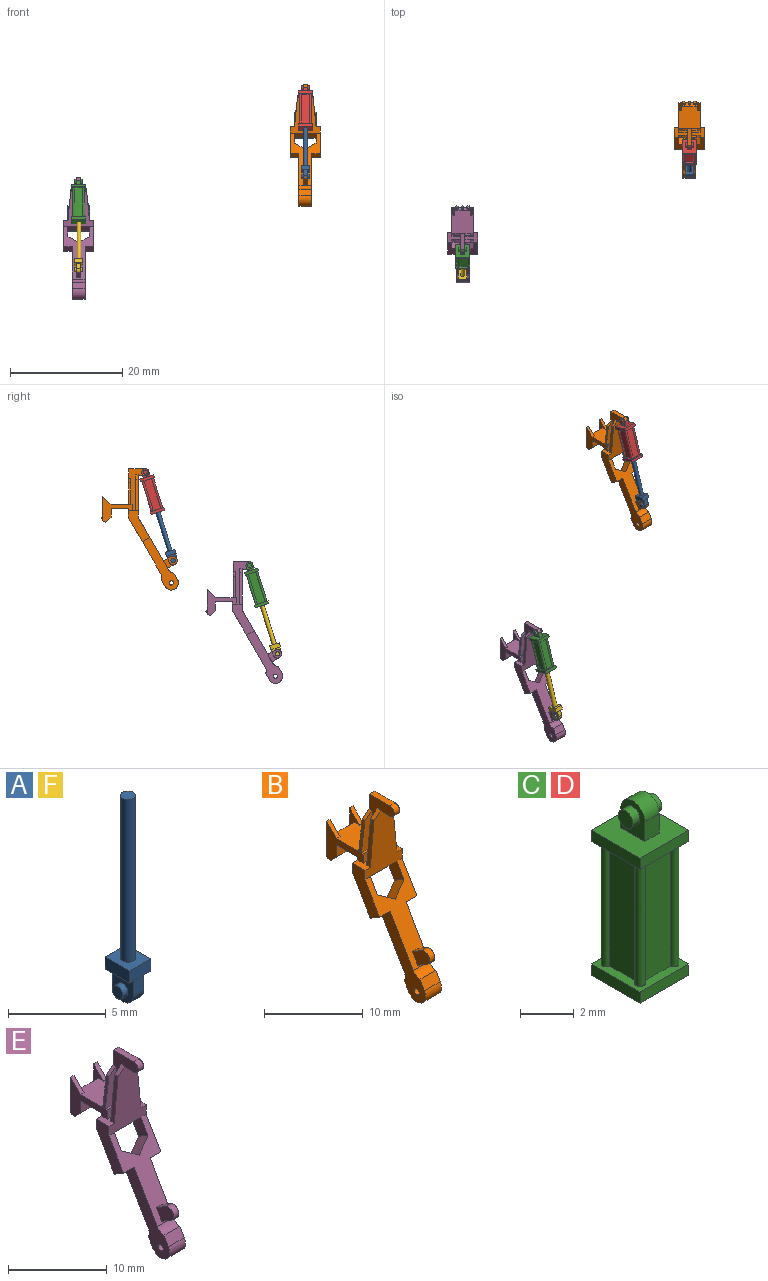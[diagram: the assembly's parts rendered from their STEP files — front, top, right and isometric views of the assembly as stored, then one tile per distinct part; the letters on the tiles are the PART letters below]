
ASSEMBLY  parts=6 mates=10
PART A: 17 faces, bbox 1.5x1.8x12.7 mm
  f0: plane 1.78x1.52mm, normal (0,0,-1), area 1.5mm2, adj f1,f2,f3,f4,f8,f9,f10,f11
  f1: plane 1.78x0.76mm, normal (-1,0,0), area 1.4mm2, adj f0,f2,f4,f5
  f2: plane 1.52x0.76mm, normal (0,-1,0), area 1.2mm2, adj f0,f1,f3,f5
  f3: plane 1.78x0.76mm, normal (1,0,0), area 1.4mm2, adj f0,f2,f4,f5
  f4: plane 1.52x0.76mm, normal (0,1,0), area 1.2mm2, adj f0,f1,f3,f5
  f5: plane 1.78x1.52mm, normal (0,0,1), area 2.3mm2, adj f1,f2,f3,f4,f6
  f6: cylinder r=0.38mm len=10.16mm, axis (0,0,-1), area 24.3mm2, adj f5,f7
  f7: plane 0.76x0.76mm, normal (0,0,1), area 0.5mm2, adj f6
  f8: plane 1.78x1.52mm, normal (-1,0,0), area 2mm2, adj f0,f9,f11,f12,f15
  f9: plane 1.02x0.76mm, normal (0,1,0), area 0.8mm2, adj f0,f8,f10,f12
  f10: plane 1.78x1.52mm, normal (1,0,0), area 2mm2, adj f0,f9,f11,f12,f14
  f11: plane 1.02x0.76mm, normal (0,-1,0), area 0.8mm2, adj f0,f8,f10,f12
  f12: cylinder r=0.76mm len=1.52mm, axis (1,0,0), area 1.8mm2, adj f8,f9,f10,f11
  f13: plane 0.76x0.76mm, normal (1,0,0), area 0.5mm2, adj f14
  f14: cylinder r=0.38mm len=0.76mm, axis (-1,0,0), area 0.9mm2, adj f10,f13
  f15: cylinder r=0.38mm len=0.76mm, axis (-1,0,0), area 0.9mm2, adj f8,f16
  f16: plane 0.76x0.76mm, normal (-1,0,0), area 0.5mm2, adj f15
PART B: 86 faces, bbox 5.3x13.7x21.6 mm
  f0: plane 10.13x5.85mm, normal (0,0.87,-0.5), area 31.9mm2, adj f12,f15,f26,f27,f28,f29,f30,f31
  f1: plane 9.35x5.4mm, normal (0,-0.87,0.5), area 26mm2, adj f12,f22,f26,f27,f28,f29,f30,f31
  f2: plane 2.92x0.76mm, normal (0,0,1), area 2.2mm2, adj f19,f20,f23,f79
  f3: plane 4.4x0.51mm, normal (0,1,0), area 2.2mm2, adj f7,f53,f54,f57
  f4: plane 2.79x2.29mm, normal (0,1,0), area 6.4mm2, adj f5,f6,f53,f55
  f5: plane 2.79x0.68mm, normal (0,0.71,0.71), area 2.2mm2, adj f4,f53,f55,f57,f58,f59,f60,f61
  f6: plane 3.94x3.81mm, normal (0,0,1), area 14.2mm2, adj f4,f7,f8,f53,f54,f55,f56,f79
  f7: plane 5.25x4.62mm, normal (-1,0,0), area 8.3mm2, adj f3,f6,f11,f14,f15,f16,f17,f25
  f8: plane 5.25x4.62mm, normal (1,0,0), area 8.3mm2, adj f6,f13,f15,f16,f17,f18,f24,f49
  f9: plane 4.57x1.52mm, normal (0,-1,0), area 5.2mm2, adj f18,f20,f49,f50
  f10: plane 4.57x1.52mm, normal (0,-1,0), area 5.2mm2, adj f11,f19,f47,f48
  f11: plane 1.52x0.25mm, normal (0,0,1), area 0.4mm2, adj f7,f10,f14,f19
  f12: plane 1.52x1.33mm, normal (0,-0.5,-0.87), area 2.3mm2, adj f0,f1,f27,f28
  f13: plane 1.52x1.14mm, normal (0,-1,0), area 1.7mm2, adj f8,f18,f20,f24
  f14: plane 1.52x1.14mm, normal (0,-1,0), area 1.7mm2, adj f7,f11,f19,f25
  f15: plane 5.33x1.52mm, normal (0,1,0), area 7.5mm2, adj f0,f7,f8,f16,f24,f25,f26,f27
  f16: plane 3.81x3.05mm, normal (0,0,-1), area 11.6mm2, adj f7,f8,f15,f17
  f17: plane 3.81x1.52mm, normal (0,-1,0), area 5.8mm2, adj f7,f8,f16,f52
  f18: plane 1.52x0.25mm, normal (0,0,1), area 0.4mm2, adj f8,f9,f13,f20
  f19: plane 7.49x3.56mm, normal (-1,0,0), area 8.9mm2, adj f2,f10,f11,f14,f21,f22,f23,f25
  f20: plane 7.49x3.56mm, normal (1,0,0), area 8.9mm2, adj f2,f9,f13,f18,f21,f22,f23,f24
  f21: plane 1.27x0.76mm, normal (0,0,-1), area 1mm2, adj f19,f20,f22,f23
  f22: plane 7.49x5.33mm, normal (0,-1,0), area 25.5mm2, adj f1,f19,f20,f21,f24,f25,f26,f27
  f23: cylinder r=0.64mm len=1.27mm, axis (1,0,0), area 1.5mm2, adj f2,f19,f20,f21
  f24: plane 2.29x1.78mm, normal (0,0,1), area 2.1mm2, adj f8,f13,f15,f20,f22,f27,f41,f45
  f25: plane 2.29x1.78mm, normal (0,0,1), area 2.1mm2, adj f7,f14,f15,f19,f22,f26,f42,f44
  f26: plane 5.54x3.87mm, normal (-1,0,0), area 9.2mm2, adj f0,f1,f15,f22,f25,f29
  f27: plane 5.54x3.87mm, normal (1,0,0), area 9.2mm2, adj f0,f1,f12,f15,f22,f24
  f28: plane 9.35x6.39mm, normal (1,0,0), area 17.3mm2, adj f0,f1,f12,f80,f81,f82,f83,f84
  f29: plane 1.52x1.33mm, normal (0,-0.5,-0.87), area 2.3mm2, adj f0,f1,f26,f30
  f30: plane 9.35x6.39mm, normal (-1,0,0), area 17.3mm2, adj f0,f1,f29,f80,f81,f82,f83,f84
  f31: plane 2x1.93mm, normal (0.57,0.41,0.71), area 3.6mm2, adj f0,f1,f32,f35
  f32: plane 2.53x2.35mm, normal (1,0,0), area 3.1mm2, adj f0,f1,f31,f33
  f33: plane 3.81x1.33mm, normal (0,-0.5,-0.87), area 5.9mm2, adj f0,f22,f32,f34
  f34: plane 2.53x2.35mm, normal (-1,0,0), area 3.1mm2, adj f0,f1,f33,f35
  f35: plane 2x1.93mm, normal (-0.57,0.41,0.71), area 3.6mm2, adj f0,f1,f31,f34
  f36: plane 1.32x0.76mm, normal (0,0.5,0.87), area 1.2mm2, adj f1,f37,f39,f40
  f37: cylinder r=0.76mm len=1.42mm, axis (-1,0,0), area 1.8mm2, adj f36,f38,f39,f40
  f38: plane 1.32x0.76mm, normal (0,-0.5,-0.87), area 1.2mm2, adj f1,f37,f39,f40
  f39: plane 2.46x2.18mm, normal (1,0,0), area 3.2mm2, adj f1,f36,f37,f38
  f40: plane 2.46x2.18mm, normal (-1,0,0), area 3.2mm2, adj f1,f36,f37,f38
  f41: plane 6.35x1.52mm, normal (0,1,0), area 7.3mm2, adj f20,f24,f45,f46
  f42: plane 6.35x1.52mm, normal (0,1,0), area 7.3mm2, adj f19,f25,f43,f44
  f43: plane 0.98x0.81mm, normal (-0.63,0,0.77), area 0.6mm2, adj f19,f22,f42,f44
  f44: plane 5.54x0.54mm, normal (-1,0,0.1), area 2.8mm2, adj f22,f25,f42,f43
  f45: plane 5.54x0.54mm, normal (1,0,0.1), area 2.8mm2, adj f22,f24,f41,f46
  f46: plane 0.98x0.81mm, normal (0.63,0,0.77), area 0.6mm2, adj f20,f22,f41,f45
  f47: plane 1.01x0.77mm, normal (-0.61,0,0.8), area 0.5mm2, adj f10,f19,f48,f79
  f48: plane 3.8x0.51mm, normal (-0.99,0,0.13), area 1.5mm2, adj f7,f10,f47,f79
  f49: plane 3.8x0.51mm, normal (0.99,0,0.13), area 1.5mm2, adj f8,f9,f50,f79
  f50: plane 1.01x0.77mm, normal (0.61,0,0.8), area 0.5mm2, adj f9,f20,f49,f79
  f51: plane 4.4x0.51mm, normal (0,1,0), area 2.2mm2, adj f8,f55,f56,f57
  f52: plane 3.81x0.9mm, normal (0,-0.71,-0.71), area 4.8mm2, adj f7,f8,f17,f57
  f53: plane 4.4x1.44mm, normal (1,0,0), area 2.8mm2, adj f3,f4,f5,f6,f54
  f54: plane 1.44x1.44mm, normal (0,-0.71,0.71), area 1mm2, adj f3,f6,f7,f53
  f55: plane 4.4x1.44mm, normal (-1,0,0), area 2.8mm2, adj f4,f5,f6,f51,f56
  f56: plane 1.44x1.44mm, normal (0,-0.71,0.71), area 1mm2, adj f6,f8,f51,f55
  f57: plane 3.81x0.54mm, normal (0,0.38,-0.92), area 2.2mm2, adj f3,f5,f7,f8,f51,f52
  f58: plane 0.51x0.51mm, normal (0.87,-0.35,0.35), area 0.1mm2, adj f5,f59,f63,f64
  f59: plane 0.36x0.36mm, normal (0,-0.71,0.71), area 0.1mm2, adj f5,f58,f60,f64
  f60: plane 0.51x0.51mm, normal (-0.87,-0.35,0.35), area 0.1mm2, adj f5,f59,f61,f64
  f61: plane 0.51x0.51mm, normal (-0.87,0.35,-0.35), area 0.1mm2, adj f5,f60,f62,f64
  f62: plane 0.36x0.36mm, normal (0,0.71,-0.71), area 0.1mm2, adj f5,f61,f63,f64
  f63: plane 0.51x0.51mm, normal (0.87,0.35,-0.35), area 0.1mm2, adj f5,f58,f62,f64
  f64: plane 0.51x0.31mm, normal (0,0.71,0.71), area 0.2mm2, adj f58,f59,f60,f61,f62,f63
  f65: plane 0.45x0.45mm, normal (0.5,0.61,-0.61), area 0.1mm2, adj f5,f66,f70,f71
  f66: plane 0.54x0.54mm, normal (1,0,0), area 0.1mm2, adj f5,f65,f67,f71
  f67: plane 0.45x0.45mm, normal (0.5,-0.61,0.61), area 0.1mm2, adj f5,f66,f68,f71
  f68: plane 0.45x0.45mm, normal (-0.5,-0.61,0.61), area 0.1mm2, adj f5,f67,f69,f71
  f69: plane 0.54x0.54mm, normal (-1,0,0), area 0.1mm2, adj f5,f68,f70,f71
  f70: plane 0.45x0.45mm, normal (-0.5,0.61,-0.61), area 0.1mm2, adj f5,f65,f69,f71
  f71: plane 0.44x0.36mm, normal (0,0.71,0.71), area 0.2mm2, adj f65,f66,f67,f68,f69,f70
  f72: plane 0.45x0.45mm, normal (0.5,0.61,-0.61), area 0.1mm2, adj f5,f73,f77,f78
  f73: plane 0.54x0.54mm, normal (1,0,0), area 0.1mm2, adj f5,f72,f74,f78
  f74: plane 0.45x0.45mm, normal (0.5,-0.61,0.61), area 0.1mm2, adj f5,f73,f75,f78
  f75: plane 0.45x0.45mm, normal (-0.5,-0.61,0.61), area 0.1mm2, adj f5,f74,f76,f78
  f76: plane 0.54x0.54mm, normal (-1,0,0), area 0.1mm2, adj f5,f75,f77,f78
  f77: plane 0.45x0.45mm, normal (-0.5,0.61,-0.61), area 0.1mm2, adj f5,f72,f76,f78
  f78: plane 0.44x0.36mm, normal (0,0.71,0.71), area 0.2mm2, adj f72,f73,f74,f75,f76,f77
  f79: plane 6.35x3.81mm, normal (0,1,0), area 15.3mm2, adj f2,f6,f19,f20,f47,f48,f49,f50
  f80: plane 2.29x1.1mm, normal (0,-0.87,0.5), area 2.9mm2, adj f28,f30,f82,f84
  f81: plane 2.29x1.1mm, normal (0,0.87,-0.5), area 2.9mm2, adj f28,f30,f82,f83
  f82: cylinder r=1.27mm len=2.37mm, axis (1,0,0), area 9.1mm2, adj f28,f30,f80,f81
  f83: cylinder r=1.27mm len=2.29mm, axis (1,0,0), area 2.6mm2, adj f0,f28,f30,f81
  f84: cylinder r=1.27mm len=2.29mm, axis (-1,0,0), area 2.7mm2, adj f1,f28,f30,f80
  f85: cylinder r=0.38mm len=2.29mm, axis (-1,0,0), area 5.5mm2, adj f28,f30
PART C: 31 faces, bbox 2.5x2.5x8.1 mm
  f0: plane 2.54x0.51mm, normal (1,0,0), area 1.3mm2, adj f1,f3,f4,f5
  f1: plane 2.54x0.51mm, normal (0,1,0), area 1.3mm2, adj f0,f2,f4,f5
  f2: plane 2.54x0.51mm, normal (-1,0,0), area 1.3mm2, adj f1,f3,f4,f5
  f3: plane 2.54x0.51mm, normal (0,-1,0), area 1.3mm2, adj f0,f2,f4,f5
  f4: plane 2.54x2.54mm, normal (0,0,1), area 2.9mm2, adj f0,f1,f2,f3,f6,f7,f8,f9
  f5: plane 2.54x2.54mm, normal (0,0,-1), area 6mm2, adj f0,f1,f2,f3,f25
  f6: plane 5.59x1.4mm, normal (0,1,0), area 7.8mm2, adj f4,f12,f13,f14
  f7: plane 5.59x1.4mm, normal (-1,0,0), area 7.8mm2, adj f4,f10,f13,f14
  f8: plane 5.59x1.4mm, normal (1,0,0), area 7.8mm2, adj f4,f11,f12,f14
  f9: plane 5.59x1.4mm, normal (0,-1,0), area 7.8mm2, adj f4,f10,f11,f14
  f10: cylinder r=0.19mm len=5.59mm, axis (0,0,-1), area 5mm2, adj f4,f7,f9,f14
  f11: cylinder r=0.19mm len=5.59mm, axis (0,0,-1), area 5mm2, adj f4,f8,f9,f14
  f12: cylinder r=0.19mm len=5.59mm, axis (0,0,-1), area 5mm2, adj f4,f6,f8,f14
  f13: cylinder r=0.19mm len=5.59mm, axis (0,0,-1), area 5mm2, adj f4,f6,f7,f14
  f14: plane 2.54x2.54mm, normal (0,0,-1), area 2.9mm2, adj f6,f7,f8,f9,f10,f11,f12,f13
  f15: plane 2.54x0.51mm, normal (1,0,0), area 1.3mm2, adj f14,f16,f18,f19
  f16: plane 2.54x0.51mm, normal (0,1,0), area 1.3mm2, adj f14,f15,f17,f19
  f17: plane 2.54x0.51mm, normal (-1,0,0), area 1.3mm2, adj f14,f16,f18,f19
  f18: plane 2.54x0.51mm, normal (0,-1,0), area 1.3mm2, adj f14,f15,f17,f19
  f19: plane 2.54x2.54mm, normal (0,0,1), area 5.5mm2, adj f15,f16,f17,f18,f20,f21,f22,f23
  f20: plane 1.52x1.27mm, normal (-1,0,0), area 1.3mm2, adj f19,f21,f23,f24,f29
  f21: plane 0.89x0.76mm, normal (0,-1,0), area 0.7mm2, adj f19,f20,f22,f24
  f22: plane 1.52x1.27mm, normal (1,0,0), area 1.3mm2, adj f19,f21,f23,f24,f28
  f23: plane 0.89x0.76mm, normal (0,1,0), area 0.7mm2, adj f19,f20,f22,f24
  f24: cylinder r=0.64mm len=1.27mm, axis (1,0,0), area 1.5mm2, adj f20,f21,f22,f23
  f25: cylinder r=0.38mm len=0.76mm, axis (0,0,-1), area 0.6mm2, adj f5,f26
  f26: plane 0.76x0.76mm, normal (0,0,-1), area 0.5mm2, adj f25
  f27: plane 0.76x0.76mm, normal (1,0,0), area 0.5mm2, adj f28
  f28: cylinder r=0.38mm len=0.76mm, axis (-1,0,0), area 0.9mm2, adj f22,f27
  f29: cylinder r=0.38mm len=0.76mm, axis (-1,0,0), area 0.9mm2, adj f20,f30
  f30: plane 0.76x0.76mm, normal (-1,0,0), area 0.5mm2, adj f29
PART D: same geometry as C
PART E: 86 faces, bbox 5.3x13.7x21.6 mm
  f0: plane 10.13x5.85mm, normal (0,0.87,-0.5), area 31.9mm2, adj f12,f15,f26,f27,f28,f29,f30,f31
  f1: plane 9.35x5.4mm, normal (0,-0.87,0.5), area 26mm2, adj f12,f22,f26,f27,f28,f29,f30,f31
  f2: plane 2.92x0.76mm, normal (0,0,1), area 2.2mm2, adj f19,f20,f23,f79
  f3: plane 4.4x0.51mm, normal (0,1,0), area 2.2mm2, adj f7,f53,f54,f57
  f4: plane 2.79x2.29mm, normal (0,1,0), area 6.4mm2, adj f5,f6,f53,f55
  f5: plane 2.79x0.68mm, normal (0,0.71,0.71), area 2.2mm2, adj f4,f53,f55,f57,f58,f59,f60,f61
  f6: plane 3.94x3.81mm, normal (0,0,1), area 14.2mm2, adj f4,f7,f8,f53,f54,f55,f56,f79
  f7: plane 5.25x4.62mm, normal (1,0,0), area 8.3mm2, adj f3,f6,f11,f14,f15,f16,f17,f25
  f8: plane 5.25x4.62mm, normal (-1,0,0), area 8.3mm2, adj f6,f13,f15,f16,f17,f18,f24,f49
  f9: plane 4.57x1.52mm, normal (0,-1,0), area 5.2mm2, adj f18,f20,f49,f50
  f10: plane 4.57x1.52mm, normal (0,-1,0), area 5.2mm2, adj f11,f19,f47,f48
  f11: plane 1.52x0.25mm, normal (0,0,1), area 0.4mm2, adj f7,f10,f14,f19
  f12: plane 1.52x1.33mm, normal (0,-0.5,-0.87), area 2.3mm2, adj f0,f1,f27,f28
  f13: plane 1.52x1.14mm, normal (0,-1,0), area 1.7mm2, adj f8,f18,f20,f24
  f14: plane 1.52x1.14mm, normal (0,-1,0), area 1.7mm2, adj f7,f11,f19,f25
  f15: plane 5.33x1.52mm, normal (0,1,0), area 7.5mm2, adj f0,f7,f8,f16,f24,f25,f26,f27
  f16: plane 3.81x3.05mm, normal (0,0,-1), area 11.6mm2, adj f7,f8,f15,f17
  f17: plane 3.81x1.52mm, normal (0,-1,0), area 5.8mm2, adj f7,f8,f16,f52
  f18: plane 1.52x0.25mm, normal (0,0,1), area 0.4mm2, adj f8,f9,f13,f20
  f19: plane 7.49x3.56mm, normal (1,0,0), area 8.9mm2, adj f2,f10,f11,f14,f21,f22,f23,f25
  f20: plane 7.49x3.56mm, normal (-1,0,0), area 8.9mm2, adj f2,f9,f13,f18,f21,f22,f23,f24
  f21: plane 1.27x0.76mm, normal (0,0,-1), area 1mm2, adj f19,f20,f22,f23
  f22: plane 7.49x5.33mm, normal (0,-1,0), area 25.5mm2, adj f1,f19,f20,f21,f24,f25,f26,f27
  f23: cylinder r=0.64mm len=1.27mm, axis (-1,0,0), area 1.5mm2, adj f2,f19,f20,f21
  f24: plane 2.29x1.78mm, normal (0,0,1), area 2.1mm2, adj f8,f13,f15,f20,f22,f27,f41,f45
  f25: plane 2.29x1.78mm, normal (0,0,1), area 2.1mm2, adj f7,f14,f15,f19,f22,f26,f42,f44
  f26: plane 5.54x3.87mm, normal (1,0,0), area 9.2mm2, adj f0,f1,f15,f22,f25,f29
  f27: plane 5.54x3.87mm, normal (-1,0,0), area 9.2mm2, adj f0,f1,f12,f15,f22,f24
  f28: plane 9.35x6.39mm, normal (-1,0,0), area 17.3mm2, adj f0,f1,f12,f80,f81,f82,f83,f84
  f29: plane 1.52x1.33mm, normal (0,-0.5,-0.87), area 2.3mm2, adj f0,f1,f26,f30
  f30: plane 9.35x6.39mm, normal (1,0,0), area 17.3mm2, adj f0,f1,f29,f80,f81,f82,f83,f84
  f31: plane 2x1.93mm, normal (-0.57,0.41,0.71), area 3.6mm2, adj f0,f1,f32,f35
  f32: plane 2.53x2.35mm, normal (-1,0,0), area 3.1mm2, adj f0,f1,f31,f33
  f33: plane 3.81x1.33mm, normal (0,-0.5,-0.87), area 5.9mm2, adj f0,f22,f32,f34
  f34: plane 2.53x2.35mm, normal (1,0,0), area 3.1mm2, adj f0,f1,f33,f35
  f35: plane 2x1.93mm, normal (0.57,0.41,0.71), area 3.6mm2, adj f0,f1,f31,f34
  f36: plane 1.32x0.76mm, normal (0,0.5,0.87), area 1.2mm2, adj f1,f37,f39,f40
  f37: cylinder r=0.76mm len=1.42mm, axis (1,0,0), area 1.8mm2, adj f36,f38,f39,f40
  f38: plane 1.32x0.76mm, normal (0,-0.5,-0.87), area 1.2mm2, adj f1,f37,f39,f40
  f39: plane 2.46x2.18mm, normal (-1,0,0), area 3.2mm2, adj f1,f36,f37,f38
  f40: plane 2.46x2.18mm, normal (1,0,0), area 3.2mm2, adj f1,f36,f37,f38
  f41: plane 6.35x1.52mm, normal (0,1,0), area 7.3mm2, adj f20,f24,f45,f46
  f42: plane 6.35x1.52mm, normal (0,1,0), area 7.3mm2, adj f19,f25,f43,f44
  f43: plane 0.98x0.81mm, normal (0.63,0,0.77), area 0.6mm2, adj f19,f22,f42,f44
  f44: plane 5.54x0.54mm, normal (1,0,0.1), area 2.8mm2, adj f22,f25,f42,f43
  f45: plane 5.54x0.54mm, normal (-1,0,0.1), area 2.8mm2, adj f22,f24,f41,f46
  f46: plane 0.98x0.81mm, normal (-0.63,0,0.77), area 0.6mm2, adj f20,f22,f41,f45
  f47: plane 1.01x0.77mm, normal (0.61,0,0.8), area 0.5mm2, adj f10,f19,f48,f79
  f48: plane 3.8x0.51mm, normal (0.99,0,0.13), area 1.5mm2, adj f7,f10,f47,f79
  f49: plane 3.8x0.51mm, normal (-0.99,0,0.13), area 1.5mm2, adj f8,f9,f50,f79
  f50: plane 1.01x0.77mm, normal (-0.61,0,0.8), area 0.5mm2, adj f9,f20,f49,f79
  f51: plane 4.4x0.51mm, normal (0,1,0), area 2.2mm2, adj f8,f55,f56,f57
  f52: plane 3.81x0.9mm, normal (0,-0.71,-0.71), area 4.8mm2, adj f7,f8,f17,f57
  f53: plane 4.4x1.44mm, normal (-1,0,0), area 2.8mm2, adj f3,f4,f5,f6,f54
  f54: plane 1.44x1.44mm, normal (0,-0.71,0.71), area 1mm2, adj f3,f6,f7,f53
  f55: plane 4.4x1.44mm, normal (1,0,0), area 2.8mm2, adj f4,f5,f6,f51,f56
  f56: plane 1.44x1.44mm, normal (0,-0.71,0.71), area 1mm2, adj f6,f8,f51,f55
  f57: plane 3.81x0.54mm, normal (0,0.38,-0.92), area 2.2mm2, adj f3,f5,f7,f8,f51,f52
  f58: plane 0.51x0.51mm, normal (-0.87,-0.35,0.35), area 0.1mm2, adj f5,f59,f63,f64
  f59: plane 0.36x0.36mm, normal (0,-0.71,0.71), area 0.1mm2, adj f5,f58,f60,f64
  f60: plane 0.51x0.51mm, normal (0.87,-0.35,0.35), area 0.1mm2, adj f5,f59,f61,f64
  f61: plane 0.51x0.51mm, normal (0.87,0.35,-0.35), area 0.1mm2, adj f5,f60,f62,f64
  f62: plane 0.36x0.36mm, normal (0,0.71,-0.71), area 0.1mm2, adj f5,f61,f63,f64
  f63: plane 0.51x0.51mm, normal (-0.87,0.35,-0.35), area 0.1mm2, adj f5,f58,f62,f64
  f64: plane 0.51x0.31mm, normal (0,0.71,0.71), area 0.2mm2, adj f58,f59,f60,f61,f62,f63
  f65: plane 0.45x0.45mm, normal (-0.5,0.61,-0.61), area 0.1mm2, adj f5,f66,f70,f71
  f66: plane 0.54x0.54mm, normal (-1,0,0), area 0.1mm2, adj f5,f65,f67,f71
  f67: plane 0.45x0.45mm, normal (-0.5,-0.61,0.61), area 0.1mm2, adj f5,f66,f68,f71
  f68: plane 0.45x0.45mm, normal (0.5,-0.61,0.61), area 0.1mm2, adj f5,f67,f69,f71
  f69: plane 0.54x0.54mm, normal (1,0,0), area 0.1mm2, adj f5,f68,f70,f71
  f70: plane 0.45x0.45mm, normal (0.5,0.61,-0.61), area 0.1mm2, adj f5,f65,f69,f71
  f71: plane 0.44x0.36mm, normal (0,0.71,0.71), area 0.2mm2, adj f65,f66,f67,f68,f69,f70
  f72: plane 0.45x0.45mm, normal (-0.5,0.61,-0.61), area 0.1mm2, adj f5,f73,f77,f78
  f73: plane 0.54x0.54mm, normal (-1,0,0), area 0.1mm2, adj f5,f72,f74,f78
  f74: plane 0.45x0.45mm, normal (-0.5,-0.61,0.61), area 0.1mm2, adj f5,f73,f75,f78
  f75: plane 0.45x0.45mm, normal (0.5,-0.61,0.61), area 0.1mm2, adj f5,f74,f76,f78
  f76: plane 0.54x0.54mm, normal (1,0,0), area 0.1mm2, adj f5,f75,f77,f78
  f77: plane 0.45x0.45mm, normal (0.5,0.61,-0.61), area 0.1mm2, adj f5,f72,f76,f78
  f78: plane 0.44x0.36mm, normal (0,0.71,0.71), area 0.2mm2, adj f72,f73,f74,f75,f76,f77
  f79: plane 6.35x3.81mm, normal (0,1,0), area 15.3mm2, adj f2,f6,f19,f20,f47,f48,f49,f50
  f80: plane 2.29x1.1mm, normal (0,-0.87,0.5), area 2.9mm2, adj f28,f30,f82,f84
  f81: plane 2.29x1.1mm, normal (0,0.87,-0.5), area 2.9mm2, adj f28,f30,f82,f83
  f82: cylinder r=1.27mm len=2.37mm, axis (-1,0,0), area 9.1mm2, adj f28,f30,f80,f81
  f83: cylinder r=1.27mm len=2.29mm, axis (-1,0,0), area 2.6mm2, adj f0,f28,f30,f81
  f84: cylinder r=1.27mm len=2.29mm, axis (1,0,0), area 2.7mm2, adj f1,f28,f30,f80
  f85: cylinder r=0.38mm len=2.29mm, axis (1,0,0), area 5.5mm2, adj f28,f30
PART F: same geometry as A
PLACE A rot(axis=(-1,0,0),17.5deg) t=(9.39,-18.86,19.58)mm
PLACE B t=(14.91,-7.76,25.24)mm fixed
PLACE C rot(axis=(-1,0,0),17.5deg) t=(-57.65,-32.81,9.87)mm
PLACE D rot(axis=(-1,0,0),17.5deg) t=(-17.34,-14.26,26.48)mm
PLACE E t=(-58.92,-26.3,8.64)mm fixed
PLACE F rot(axis=(-1,0,0),17.5deg) t=(-30.92,-37.4,2.98)mm
MATE cylindrical C.f24 <-> E.f23  axis (1,0,0) through (-58.92,-29.35,16.64)mm
MATE planar A.f10 <-> B.f39  axis (1,0,0) through (-18.23,-15.67,17.77)mm
MATE cylindrical E.f37 <-> F.f12  axis (1,0,0) through (-58.92,-34.29,0.93)mm
MATE planar F.f10 <-> E.f40  axis (1,0,0) through (-58.54,-34.21,1.17)mm
MATE cylindrical C.f25 <-> F.f6  axis (0,-0.3,-0.95) through (-58.92,-31.56,9.61)mm
MATE planar D.f22 <-> B.f23  axis (1,0,0) through (-18.23,-10.88,33)mm
MATE cylindrical D.f24 <-> B.f23  axis (1,0,0) through (-18.61,-10.8,33.25)mm
MATE planar C.f22 <-> E.f23  axis (1,0,0) through (-58.54,-29.42,16.4)mm
MATE cylindrical D.f25 <-> A.f6  axis (0,-0.3,-0.95) through (-18.61,-13.05,26.1)mm
MATE cylindrical A.f12 <-> B.f37  axis (1,0,0) through (-18.61,-15.74,17.54)mm
